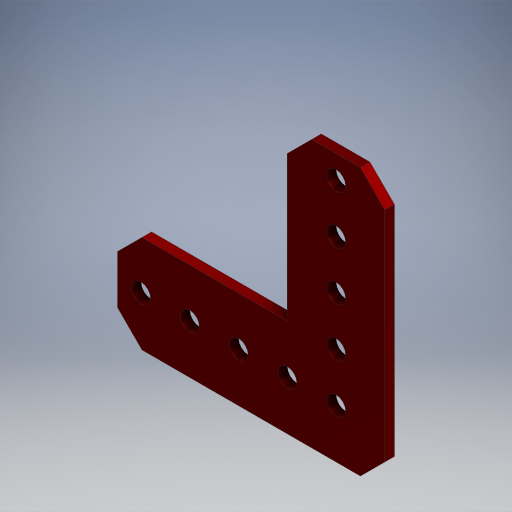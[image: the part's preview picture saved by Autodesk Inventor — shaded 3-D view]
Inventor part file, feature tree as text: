
AUTODESK INVENTOR PART (.ipt)
format: ipt  version: 2024.2 (Build 282272000, 272)  size: 282,624 bytes
history: native  units: in
note: dims shown in document units (in); Inventor stores cm internally (conversion verified against a paired STEP export)
features: chamfer x1
ambient origin geometry x8: Origin, YZ Plane, XZ Plane, XY Plane, X Axis, Y Axis, Z Axis, Center Point
bodies: Solid1 (feature_tree)
feature tree (1):
  chamfer  "Chamfer1"  [1 undecoded]
note: 1 required parameter value undecoded (feature->parameter linkage not recoverable at this tier; creation-order binding heuristic only, values carry confidence <= 0.55)
